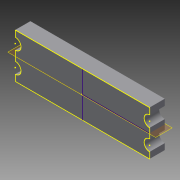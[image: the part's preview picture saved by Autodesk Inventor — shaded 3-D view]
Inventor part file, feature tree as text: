
AUTODESK INVENTOR PART (.ipt)
format: ipt  version: 2014 (Build 180170000, 170)  size: 107,008 bytes
history: native  units: mm
features: sketch x3, extrude x2, other x1, plane x1
ambient origin geometry x8: Origin, YZ Plane, XZ Plane, XY Plane, X Axis, Y Axis, Z Axis, Center Point
bodies: Volumenkörper1 (feature_tree)
feature tree (7):
  extrude  "Extrusion1"  Depth=2.35mm
  extrude  "Extrusion2"  Depth=0.8mm
  sketch  "Skizze3"  dims[d5=0.6mm d6=0.6mm d7=0.6mm d8=1.1mm d9=1.1mm d10=0.625mm d11=0.62mm d12=0.8mm d13=0.0mm]
  other  "Arbeitspunkt1"
  plane  "Arbeitsebene1"
  sketch  "Skizze1"  dims[d0=7.1mm d1=2.35mm]
  sketch  "Skizze2"  dims[d2=0.8mm d3=0.0mm d4=0.6mm]
